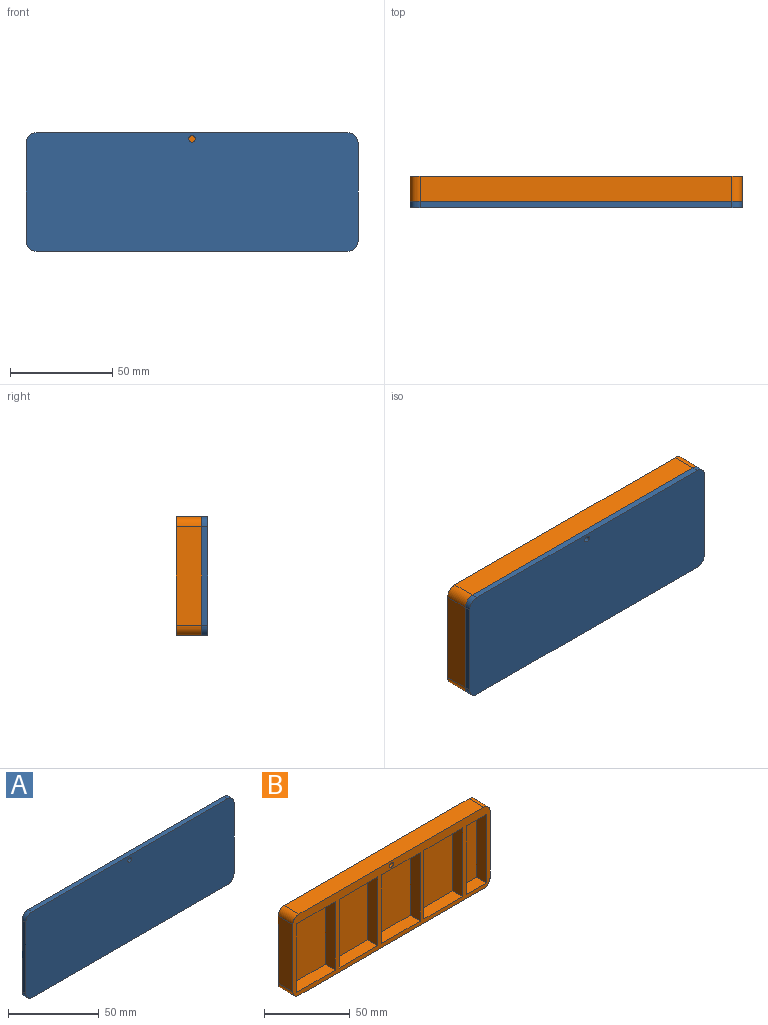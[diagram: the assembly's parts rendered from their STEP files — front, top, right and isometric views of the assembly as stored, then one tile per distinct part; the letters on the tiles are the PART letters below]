
ASSEMBLY  parts=2 mates=1
PART A: 11 faces, bbox 162.5x3x58 mm
  f0: plane 152.5x3mm, normal (0,0,1), area 457.5mm2, adj f1,f8,f9,f10
  f1: cylinder r=5mm len=5mm, axis (0,1,0), area 23.6mm2, adj f0,f2,f9,f10
  f2: plane 48x3mm, normal (-1,0,0), area 144mm2, adj f1,f3,f9,f10
  f3: cylinder r=5mm len=5mm, axis (0,1,0), area 23.6mm2, adj f2,f4,f9,f10
  f4: plane 152.5x3mm, normal (0,0,-1), area 457.5mm2, adj f3,f5,f9,f10
  f5: cylinder r=5mm len=5mm, axis (0,1,0), area 23.6mm2, adj f4,f6,f9,f10
  f6: plane 48x3mm, normal (1,0,0), area 144mm2, adj f5,f8,f9,f10
  f7: cylinder r=1.6mm len=3.2mm, axis (0,1,0), area 30.2mm2, adj f9,f10
  f8: cylinder r=5mm len=5mm, axis (0,1,0), area 23.6mm2, adj f0,f6,f9,f10
  f9: plane 162.5x58mm, normal (0,-1,0), area 9395.5mm2, adj f0,f1,f2,f3,f4,f5,f6,f7
  f10: plane 162.5x58mm, normal (0,1,0), area 9395.5mm2, adj f0,f1,f2,f3,f4,f5,f6,f7
PART B: 37 faces, bbox 162.5x12.3x58 mm
  f0: plane 16.5x8.3mm, normal (0,0,1), area 136.9mm2, adj f1,f24,f25,f28
  f1: plane 49x8.3mm, normal (1,0,0), area 406.7mm2, adj f0,f2,f25,f28
  f2: plane 16.5x8.3mm, normal (0,0,-1), area 136.9mm2, adj f1,f24,f25,f28
  f3: plane 152.5x12.3mm, normal (0,0,1), area 1875.8mm2, adj f25,f26,f33,f36
  f4: plane 48x12.3mm, normal (-1,0,0), area 590.4mm2, adj f25,f26,f33,f34
  f5: plane 152.5x12.3mm, normal (0,0,-1), area 1875.8mm2, adj f25,f26,f34,f35
  f6: plane 49x8.3mm, normal (-1,0,0), area 406.7mm2, adj f7,f20,f25,f31
  f7: plane 32x8.3mm, normal (0,0,1), area 265.6mm2, adj f6,f8,f25,f31
  f8: plane 49x8.3mm, normal (1,0,0), area 406.7mm2, adj f7,f20,f25,f31
  f9: plane 49x8.3mm, normal (-1,0,0), area 406.7mm2, adj f10,f21,f25,f30
  f10: plane 32x8.3mm, normal (0,0,1), area 265.6mm2, adj f9,f11,f25,f30
  f11: plane 49x8.3mm, normal (1,0,0), area 406.7mm2, adj f10,f21,f25,f30
  f12: plane 49x8.3mm, normal (-1,0,0), area 406.7mm2, adj f13,f22,f25,f29
  f13: plane 32x8.3mm, normal (0,0,1), area 265.6mm2, adj f12,f14,f25,f29
  f14: plane 49x8.3mm, normal (1,0,0), area 406.7mm2, adj f13,f22,f25,f29
  f15: plane 32x8.3mm, normal (0,0,1), area 265.6mm2, adj f16,f23,f25,f27
  f16: plane 49x8.3mm, normal (1,0,0), area 406.7mm2, adj f15,f17,f25,f27
  f17: plane 32x8.3mm, normal (0,0,-1), area 265.6mm2, adj f16,f23,f25,f27
  f18: cylinder r=1.6mm len=7.3mm, axis (0,1,0), area 73.4mm2, adj f25,f32
  f19: plane 48x12.3mm, normal (1,0,0), area 590.4mm2, adj f25,f26,f35,f36
  f20: plane 32x8.3mm, normal (0,0,-1), area 265.6mm2, adj f6,f8,f25,f31
  f21: plane 32x8.3mm, normal (0,0,-1), area 265.6mm2, adj f9,f11,f25,f30
  f22: plane 32x8.3mm, normal (0,0,-1), area 265.6mm2, adj f12,f14,f25,f29
  f23: plane 49x8.3mm, normal (-1,0,0), area 406.7mm2, adj f15,f17,f25,f27
  f24: plane 49x8.3mm, normal (-1,0,0), area 406.7mm2, adj f0,f2,f25,f28
  f25: plane 162.5x58mm, normal (0,-1,0), area 2315mm2, adj f0,f1,f2,f3,f4,f5,f6,f7
  f26: plane 162.5x58mm, normal (0,1,0), area 9403.5mm2, adj f3,f4,f5,f19,f33,f34,f35,f36
  f27: plane 49x32mm, normal (0,-1,0), area 1568mm2, adj f15,f16,f17,f23
  f28: plane 49x16.5mm, normal (0,-1,0), area 808.5mm2, adj f0,f1,f2,f24
  f29: plane 49x32mm, normal (0,-1,0), area 1568mm2, adj f12,f13,f14,f22
  f30: plane 49x32mm, normal (0,-1,0), area 1568mm2, adj f9,f10,f11,f21
  f31: plane 49x32mm, normal (0,-1,0), area 1568mm2, adj f6,f7,f8,f20
  f32: plane 3.2x3.2mm, normal (0,-1,0), area 8mm2, adj f18
  f33: cylinder r=5mm len=12.3mm, axis (0,1,0), area 96.6mm2, adj f3,f4,f25,f26
  f34: cylinder r=5mm len=12.3mm, axis (0,1,0), area 96.6mm2, adj f4,f5,f25,f26
  f35: cylinder r=5mm len=12.3mm, axis (0,1,0), area 96.6mm2, adj f5,f19,f25,f26
  f36: cylinder r=5mm len=12.3mm, axis (0,1,0), area 96.6mm2, adj f3,f19,f25,f26
PLACE A t=(-0.23,-75.61,-4)mm
PLACE B t=(-0.23,-63.31,-4)mm
MATE fastened B.f18 <-> A.f7  axis (0,-1,0) through (-158.95,-75.61,48)mm
